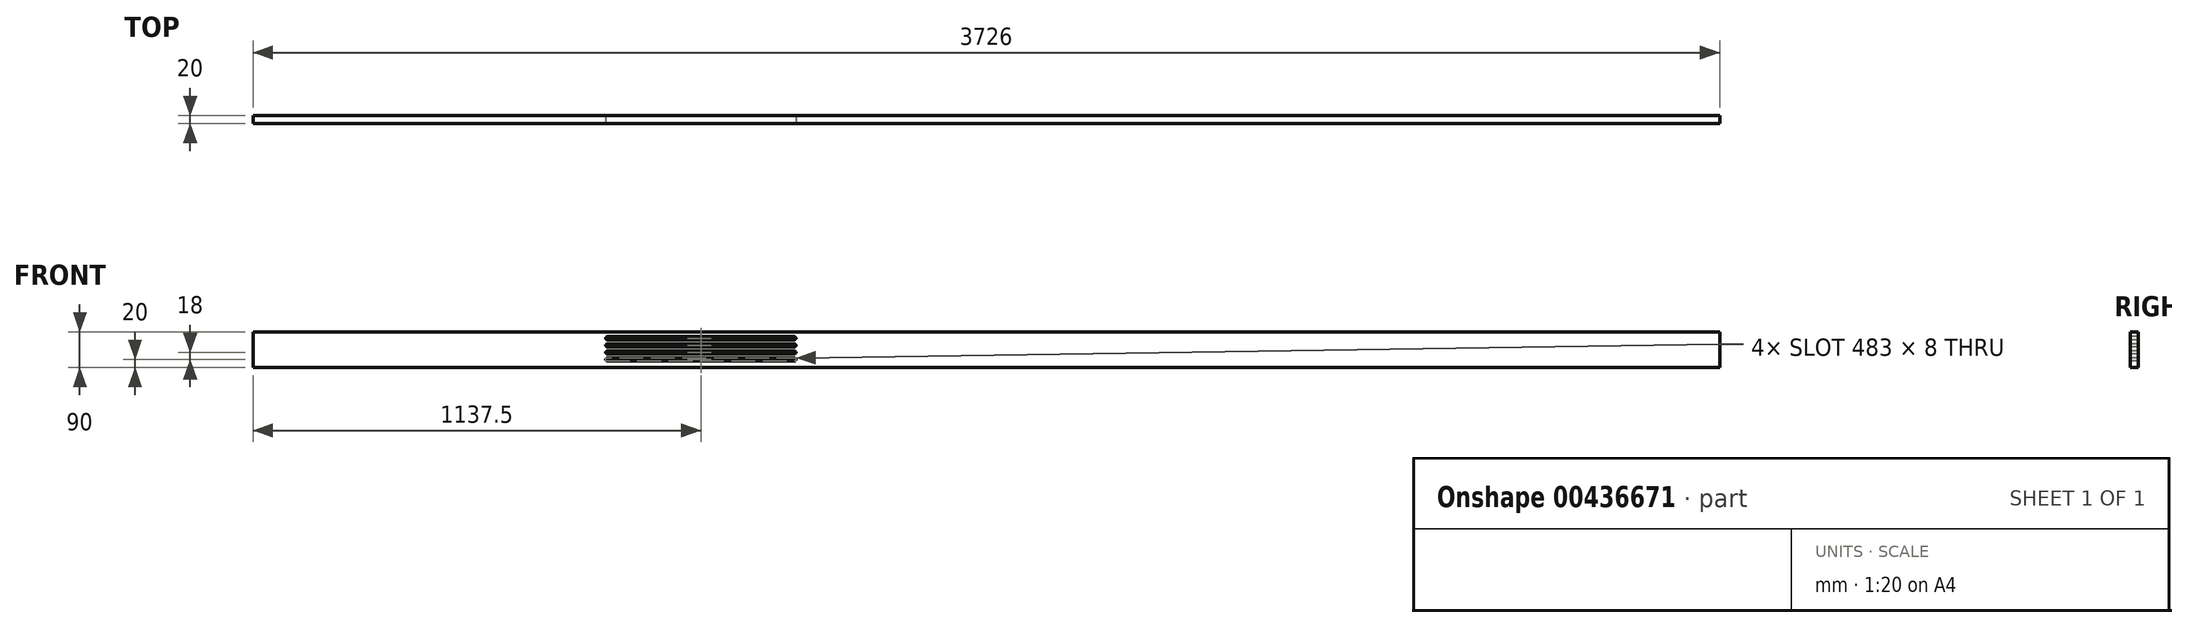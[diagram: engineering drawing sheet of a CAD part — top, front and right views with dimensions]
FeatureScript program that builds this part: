
annotation { "Feature Type Name" : "Feature", "Feature Type Description" : "" }
export const myFeature = defineFeature(function(context is Context, id is Id, definition is map)
    precondition{}
    {
        {
            var Q0;
            Q0=qCreatedBy(makeId("Right.planeOp"),FACE);
            var sketch = newSketch(context, id + "F0", { "sketchPlane" : qUnion([Q0])});
            skLineSegment(sketch, "E0.bottom", {"start": v(10, 45) * mm, "end": v(-10, 45) * mm});
            skLineSegment(sketch, "E0.top", {"start": v(10, -45) * mm, "end": v(-10, -45) * mm});
            skLineSegment(sketch, "E0.left", {"start": v(10, 45) * mm, "end": v(10, -45) * mm});
            skLineSegment(sketch, "E0.right", {"start": v(-10, 45) * mm, "end": v(-10, -45) * mm});
            skPoint(sketch, "E0.middle", {"position": v(0, 0) * mm});
            skSolve(sketch);
        }
        {
            var Q0;
            Q0 = qSketchRegion(id + "F0", true);
            extrude(context, id + "F1", {"entities" : qUnion([Q0]), "depth" : 3726 * mm});
        }
        {
            var Q0;
            Q0=makeQuery(id+"F1.opExtrude","SWEPT_FACE",FACE,{"disambiguationData":[OSD([sQuery(id+"F0.wireOp",EDGE,"E0.right")])]});
            var sketch = newSketch(context, id + "F2", { "sketchPlane" : qUnion([Q0])});
            skLineSegment(sketch, "E1.bottom", {"start": v(1375, 25) * mm, "end": v(900, 25) * mm});
            skLineSegment(sketch, "E1.top", {"start": v(1375, 33) * mm, "end": v(900, 33) * mm});
            skPoint(sketch, "E1.middle", {"position": v(1137.5, 29) * mm});
            skArc(sketch, "E2", {"start": v(900, 33) * mm, "mid": v(896, 29) * mm, "end": v(900, 25) * mm});
            skArc(sketch, "E3", {"start": v(1375, 33) * mm, "mid": v(1379, 29) * mm, "end": v(1375, 25) * mm});
            skLineSegment(sketch, "E4.0.1.0", {"start": v(1375, 15) * mm, "end": v(900, 15) * mm});
            skLineSegment(sketch, "E4.0.1.1", {"start": v(1375, 7) * mm, "end": v(900, 7) * mm});
            skArc(sketch, "E4.0.1.2", {"start": v(900, 15) * mm, "mid": v(896, 11) * mm, "end": v(900, 7) * mm});
            skArc(sketch, "E4.0.1.3", {"start": v(1375, 15) * mm, "mid": v(1379, 11) * mm, "end": v(1375, 7) * mm});
            skLineSegment(sketch, "E4.0.2.0", {"start": v(1375, -3) * mm, "end": v(900, -3) * mm});
            skLineSegment(sketch, "E4.0.2.1", {"start": v(1375, -11) * mm, "end": v(900, -11) * mm});
            skArc(sketch, "E4.0.2.2", {"start": v(900, -3) * mm, "mid": v(896, -7) * mm, "end": v(900, -11) * mm});
            skArc(sketch, "E4.0.2.3", {"start": v(1375, -3) * mm, "mid": v(1379, -7) * mm, "end": v(1375, -11) * mm});
            skLineSegment(sketch, "E4.direction1", {"start": v(900, 33) * mm, "end": v(925, 33) * mm, "construction": true});
            skLineSegment(sketch, "E4.direction2", {"start": v(900, 33) * mm, "end": v(900, 15) * mm, "construction": true});
            skLineSegment(sketch, "E5.0.0.3", {"start": v(1375, -21) * mm, "end": v(900, -21) * mm});
            skLineSegment(sketch, "E5.3.0.3", {"start": v(1375, -29) * mm, "end": v(900, -29) * mm});
            skArc(sketch, "E5.6.0.3", {"start": v(900, -21) * mm, "mid": v(896, -25) * mm, "end": v(900, -29) * mm});
            skArc(sketch, "E5.10.0.3", {"start": v(1375, -21) * mm, "mid": v(1379, -25) * mm, "end": v(1375, -29) * mm});
            skSolve(sketch);
        }
        {
            var Q0;
            Q0 = qSketchRegion(id + "F2", true);
            extrude(context, id + "F3", {"entities" : qUnion([Q0]), "operationType" : NewBodyOperationType.REMOVE, "oppositeDirection" : true, "depth" : 25 * mm});
        }
    });
